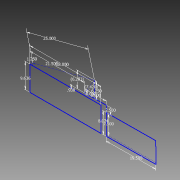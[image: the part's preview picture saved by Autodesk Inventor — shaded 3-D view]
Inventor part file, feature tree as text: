
AUTODESK INVENTOR PART (.ipt)
format: ipt  version: 2012 (Build 160160000, 160)  size: 77,824 bytes
history: native  units: in
note: dims shown in document units (in); Inventor stores cm internally (conversion verified against a paired STEP export)
features: sketch x1
ambient origin geometry x8: Origin, YZ Plane, XZ Plane, XY Plane, X Axis, Y Axis, Z Axis, Center Point
feature tree (1):
  sketch  "Sketch1"  dims[d0=28.0in d1=9.636in d5=0.938in d6=8.5in d7=2.5in d8=19.5in d9=8.074in d10=21.5in d11=7.5in d14=6.2833in d17=4.0in d18=6.25in d19=25.0in d20=7.4204in d21=1.25in]
